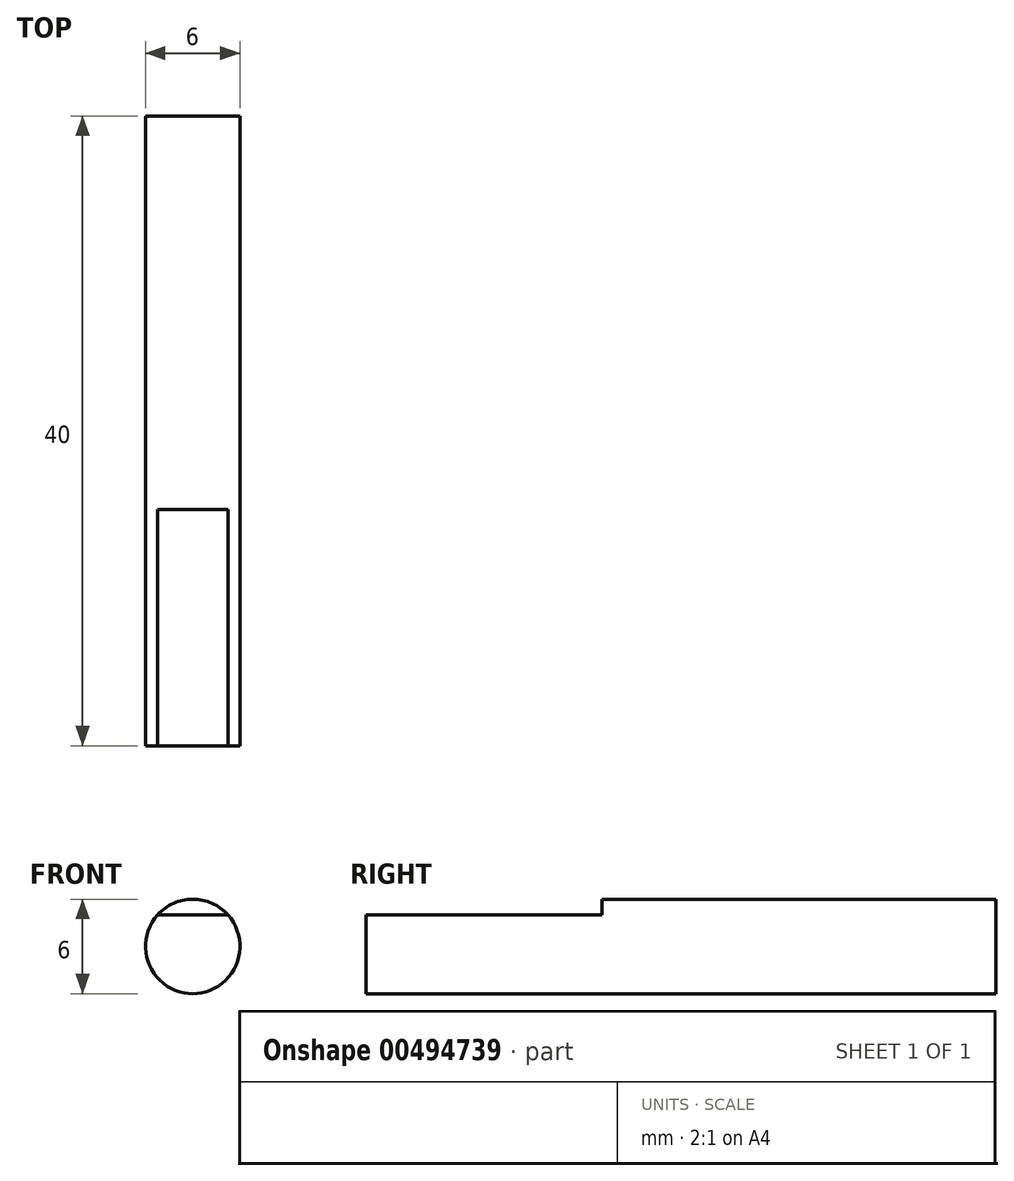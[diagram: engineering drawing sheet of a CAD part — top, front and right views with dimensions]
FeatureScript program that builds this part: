
annotation { "Feature Type Name" : "Feature", "Feature Type Description" : "" }
export const myFeature = defineFeature(function(context is Context, id is Id, definition is map)
    precondition{}
    {
        {
            var Q0;
            Q0=qCreatedBy(makeId("Front.planeOp"),FACE);
            var sketch = newSketch(context, id + "F0", { "sketchPlane" : qUnion([Q0])});
            skCircle(sketch, "E0", {"center": v(0, 0) * mm, "radius": 3 * mm});
            skSolve(sketch);
        }
        {
            var Q0;
            Q0 = qSketchRegion(id + "F0", true);
            extrude(context, id + "F1", {"entities" : qUnion([Q0]), "depth" : 40 * mm});
        }
        {
            var Q0;
            Q0=makeQuery(id+"F1.opExtrude","CAP_FACE",FACE,{"disambiguationData":[OSD([sQuery(id+"F0.wireOp",EDGE,"E0")])],"isStart":false});
            var sketch = newSketch(context, id + "F2", { "sketchPlane" : qUnion([Q0])});
            skLineSegment(sketch, "E1.top", {"start": v(3.5, 5) * mm, "end": v(-3.5, 5) * mm});
            skLineSegment(sketch, "E1.left", {"start": v(3.5, 2) * mm, "end": v(3.5, 5) * mm});
            skLineSegment(sketch, "E1.right", {"start": v(-3.5, 2) * mm, "end": v(-3.5, 5) * mm});
            skLineSegment(sketch, "E2", {"start": v(-3.5, 2) * mm, "end": v(3.5, 2) * mm});
            skSolve(sketch);
        }
        {
            var Q0;
            Q0 = qSketchRegion(id + "F2", true);
            extrude(context, id + "F3", {"entities" : qUnion([Q0]), "operationType" : NewBodyOperationType.REMOVE, "oppositeDirection" : true, "depth" : 15 * mm});
        }
    });
